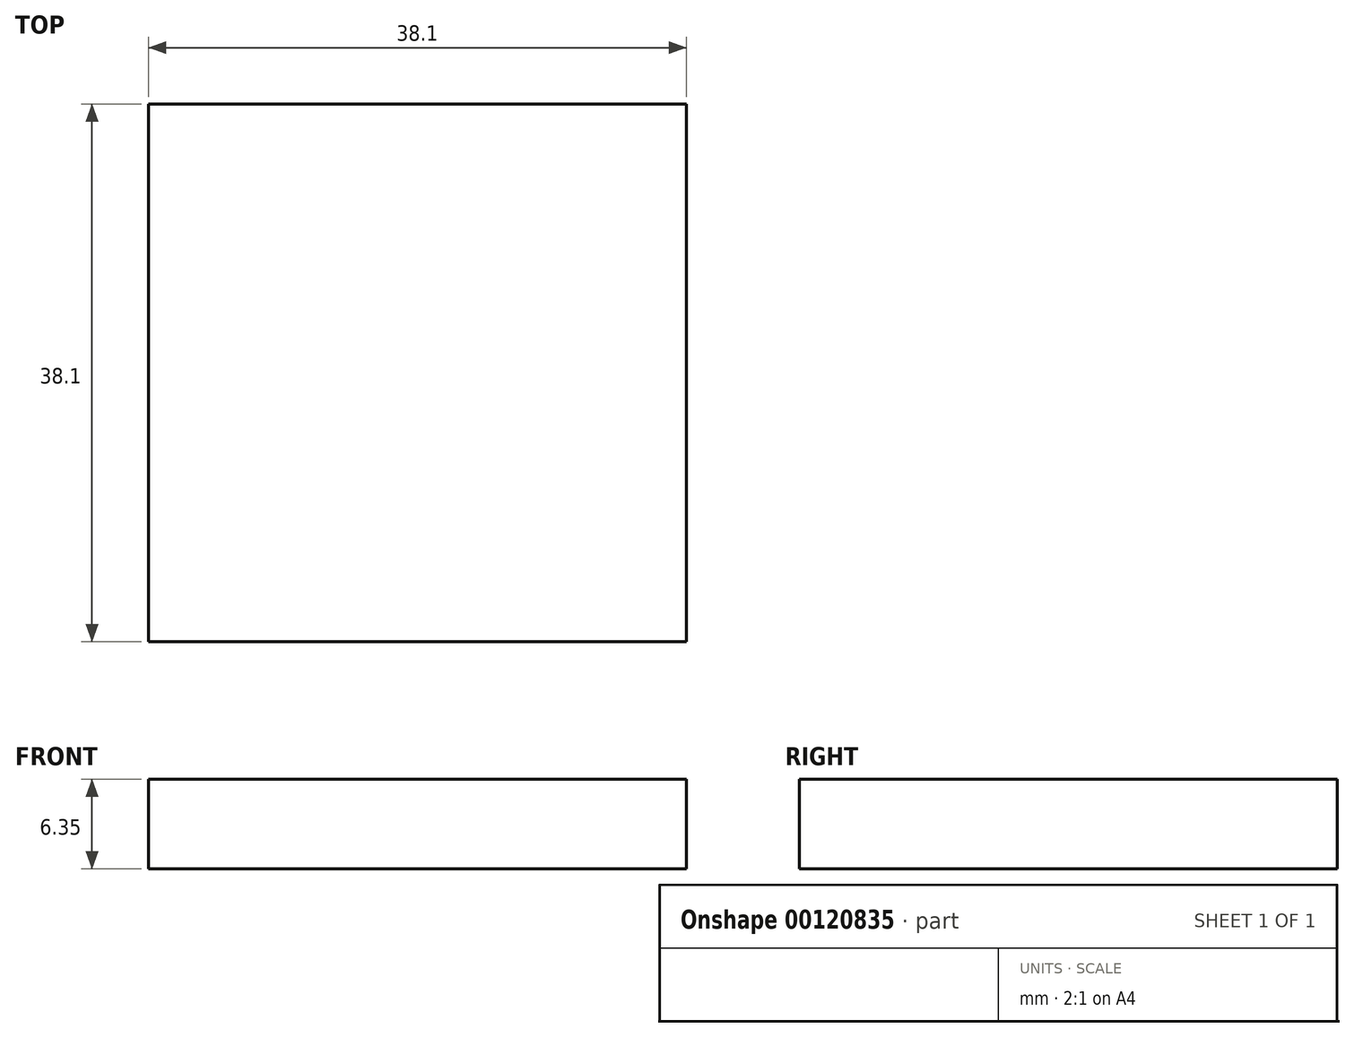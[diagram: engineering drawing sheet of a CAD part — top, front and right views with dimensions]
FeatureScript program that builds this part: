
annotation { "Feature Type Name" : "Feature", "Feature Type Description" : "" }
export const myFeature = defineFeature(function(context is Context, id is Id, definition is map)
    precondition{}
    {
        {
            var Q0;
            Q0=qCreatedBy(makeId("Top.planeOp"),FACE);
            var sketch = newSketch(context, id + "F0", { "sketchPlane" : qUnion([Q0])});
            skLineSegment(sketch, "E0.bottom", {"start": v(-19.05, 19.05) * mm, "end": v(19.05, 19.05) * mm});
            skLineSegment(sketch, "E0.top", {"start": v(-19.05, -19.05) * mm, "end": v(19.05, -19.05) * mm});
            skLineSegment(sketch, "E0.left", {"start": v(-19.05, 19.05) * mm, "end": v(-19.05, -19.05) * mm});
            skLineSegment(sketch, "E0.right", {"start": v(19.05, 19.05) * mm, "end": v(19.05, -19.05) * mm});
            skSolve(sketch);
        }
        {
            var Q0;
            Q0 = qSketchRegion(id + "F0", true);
            extrude(context, id + "F1", {"entities" : qUnion([Q0]), "depth" : 6.35 * mm});
        }
    });
